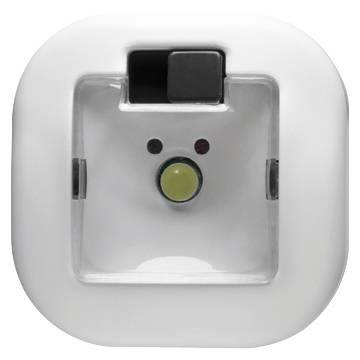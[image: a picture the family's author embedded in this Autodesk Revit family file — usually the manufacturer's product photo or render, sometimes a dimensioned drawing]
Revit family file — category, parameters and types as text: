
# Revit family: Domotics-DomesticRanges-GEWISS-CHORUS_SIGNALLING-LAMP_ANTIBLACKOUT_EXTRACTABLE
name_source: partatom
category: Apparecchi elettrici
revit_build: Autodesk Revit 2016 (Build: 20161004_0715(x64)
units: mm (PartAtom-declared; Revit-internal decimal feet)

## family parameters
Condiviso = Sì
Host = Superficie
Mantenere orientamento annotazione = Sì
Punto di calcolo locali = Sì
Quota connettore circolare = Usa diametro
Taglio con vuoti quando caricato = Sì
Tipo di parte = Normale

## types (3) — shared parameters
Altezza_lampada = 45 mm  [stored 0.147638 ft]
Catalogue = DOMOTICS
Catalogue Range = CHORUS - DOMESTIC RANGE
Description. = Extractable anti black-out lamp
Electrocod = 0781
IDF = b7dda38d-db55-4de2-a9c0-19da66d1ca7b
IDT = d6ec7bda-7e47-4b3f-94b6-7140f3f874e4
Immagine tipo = GW14661.jpg
Lamp = LED
Larghezza_lampada = 23 mm  [stored 0.0754593 ft]
Minimum autonomy = 2H
Power supply batteries = Ni - Mh
Produttore = GEWISS S.p.A.
Prospetto di default = 1219 mm
SEO = Lamp
Supply voltage = 230 V ac - 50/60 Hz
Technical sheet = https://www.gewiss.com
Tipo_ = CHORUS LAMPADE ANTIBLACK-OUT ESTRAIBILE_G : GW14661 Lampada anti black-out estraibile 230V ac 50/60Hz 2h titanio
Type: = Withdrawable
URL = https://www.gewiss.com
Version file RFA = 19.0
finitura = GEWISS NERO

## per-type parameters (varying)
| type | Colour | Descrizione | EAN code | Modello |
| GW12661 - EXT.ANTI-BLACKOUT LAMP 230VAC 50/60Hz 2h | Black | EXT.ANTI-BLACKOUT LAMP 230VAC 50/60Hz 2h | 8011564269941 | GW12661 |
| GW10661 - EXT.ANTI-BLACKOUT LAMP 230VAC 50/60Hz 2h | White | EXT.ANTI-BLACKOUT LAMP 230VAC 50/60Hz 2h | 8011564259928 | GW10661 |
| GW14661 - EXT.ANTI-BLACKOUT LAMP 230VAC 50/60Hz T. | Titanium | EXT.ANTI-BLACKOUT LAMP 230VAC 50/60Hz T. | 8011564438309 | GW14661 |

note: [stored X ft] marks values corroborated as IEEE doubles in the binary element streams (Revit-internal decimal feet)

## geometry (parser evidence)
native form markers: Sweep x2
no freeform markers — native parametric forms only
